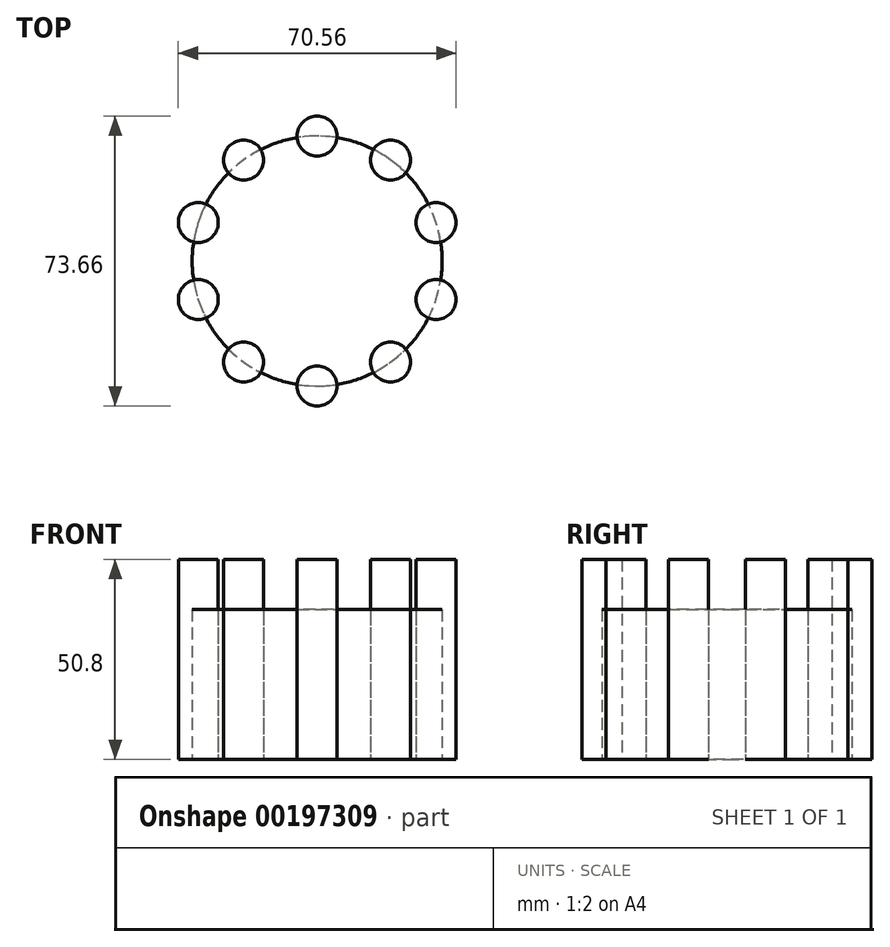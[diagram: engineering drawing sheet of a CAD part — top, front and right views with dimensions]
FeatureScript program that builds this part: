
annotation { "Feature Type Name" : "Feature", "Feature Type Description" : "" }
export const myFeature = defineFeature(function(context is Context, id is Id, definition is map)
    precondition{}
    {
        {
            var Q0;
            Q0=qCreatedBy(makeId("Top.planeOp"),FACE);
            var sketch = newSketch(context, id + "F0", { "sketchPlane" : qUnion([Q0])});
            skCircle(sketch, "E0", {"center": v(0, 0) * mm, "radius": 31.75 * mm});
            skSolve(sketch);
        }
        {
            var Q0;
            Q0=makeQuery(id+"F0.imprint","IMPRINT",FACE,{"disambiguationData":[TD([[makeQuery(id+"F0.imprint","IMPRINT",EDGE,{"derivedFrom":sQuery(id+"F0.wireOp",EDGE,"E0")}),1.0]])]});
            extrude(context, id + "F1", {"entities" : qUnion([Q0]), "depth" : 38.1 * mm});
        }
        {
            var Q0;
            Q0=qCreatedBy(makeId("Top.planeOp"),FACE);
            var sketch = newSketch(context, id + "F2", { "sketchPlane" : qUnion([Q0])});
            skCircle(sketch, "E1", {"center": v(0, 31.75) * mm, "radius": 5.08 * mm});
            skCircle(sketch, "E2.1.0", {"center": v(-18.66, 25.69) * mm, "radius": 5.08 * mm});
            skCircle(sketch, "E2.2.0", {"center": v(-30.2, 9.81) * mm, "radius": 5.08 * mm});
            skCircle(sketch, "E2.3.0", {"center": v(-30.2, -9.81) * mm, "radius": 5.08 * mm});
            skCircle(sketch, "E2.4.0", {"center": v(-18.66, -25.69) * mm, "radius": 5.08 * mm});
            skCircle(sketch, "E2.5.0", {"center": v(0, -31.75) * mm, "radius": 5.08 * mm});
            skCircle(sketch, "E2.6.0", {"center": v(18.66, -25.69) * mm, "radius": 5.08 * mm});
            skCircle(sketch, "E2.7.0", {"center": v(30.2, -9.81) * mm, "radius": 5.08 * mm});
            skCircle(sketch, "E2.8.0", {"center": v(30.2, 9.81) * mm, "radius": 5.08 * mm});
            skCircle(sketch, "E2.9.0", {"center": v(18.66, 25.69) * mm, "radius": 5.08 * mm});
            skPoint(sketch, "E2.center", {"position": v(0, 0) * mm});
            skSolve(sketch);
        }
        {
            var Q0;
            Q0=qSketchRegion(id+"F2",true);
            extrude(context, id + "F3", {"entities" : qUnion([Q0]), "depth" : 50.8 * mm});
        }
    });
